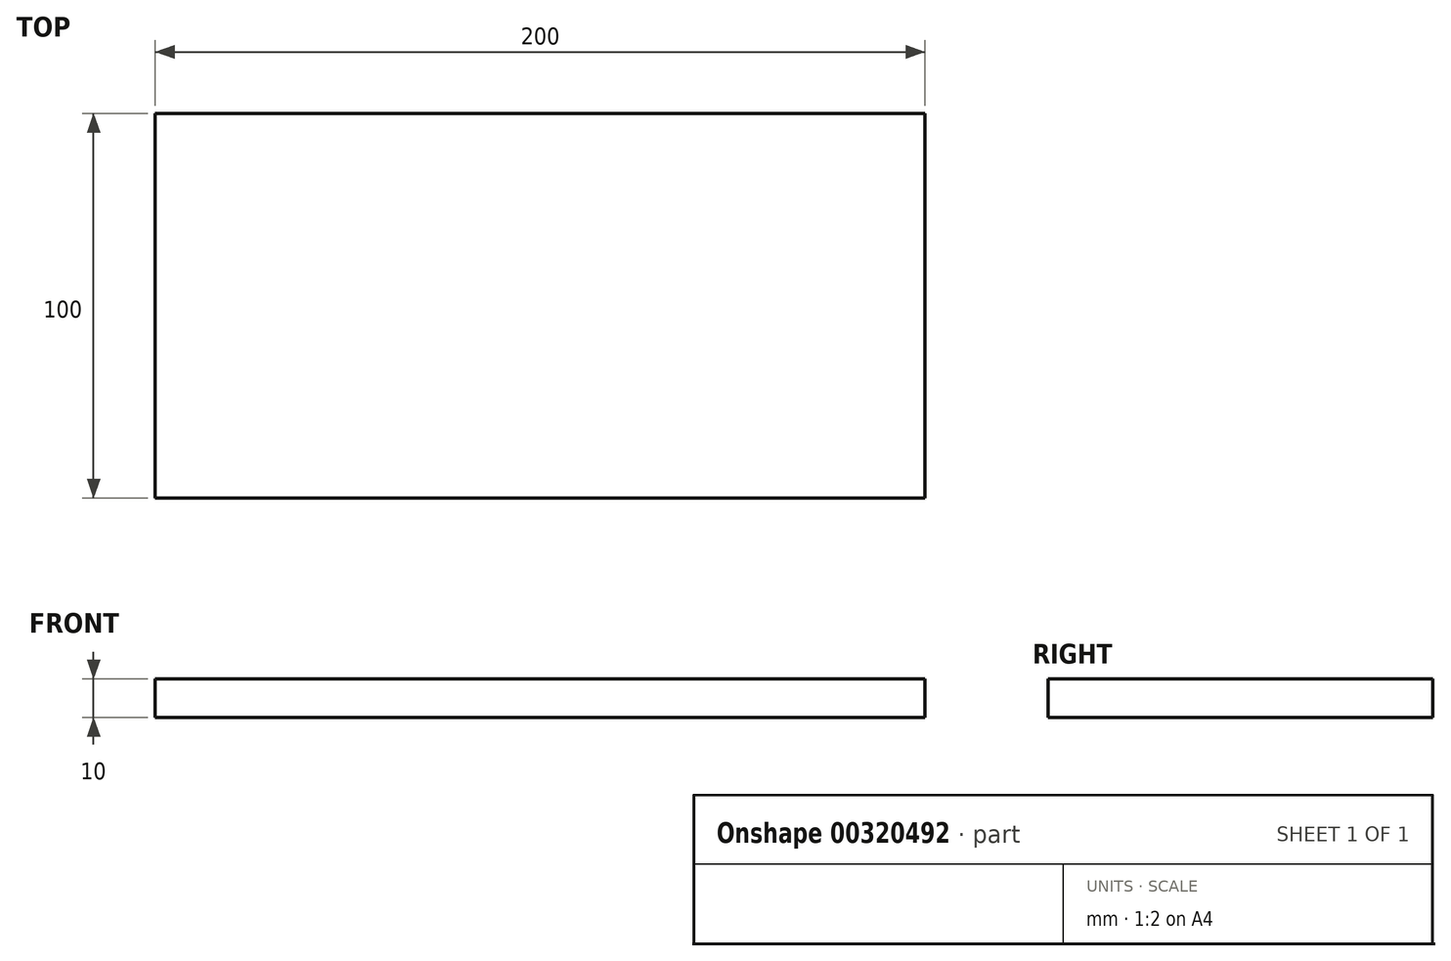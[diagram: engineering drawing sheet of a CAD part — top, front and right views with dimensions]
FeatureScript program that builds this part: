
annotation { "Feature Type Name" : "Feature", "Feature Type Description" : "" }
export const myFeature = defineFeature(function(context is Context, id is Id, definition is map)
    precondition{}
    {
        {
            var Q0;
            Q0=qCreatedBy(makeId("Top.planeOp"),FACE);
            var sketch = newSketch(context, id + "F0", { "sketchPlane" : qUnion([Q0])});
            skLineSegment(sketch, "E0.bottom", {"start": v(100, 50) * mm, "end": v(-100, 50) * mm});
            skLineSegment(sketch, "E0.top", {"start": v(100, -50) * mm, "end": v(-100, -50) * mm});
            skLineSegment(sketch, "E0.left", {"start": v(100, 50) * mm, "end": v(100, -50) * mm});
            skLineSegment(sketch, "E0.right", {"start": v(-100, 50) * mm, "end": v(-100, -50) * mm});
            skPoint(sketch, "E0.middle", {"position": v(0, 0) * mm});
            skSolve(sketch);
        }
        {
            var Q0;
            Q0 = qSketchRegion(id + "F0", true);
            extrude(context, id + "F1", {"entities" : qUnion([Q0]), "depth" : 10 * mm});
        }
    });
